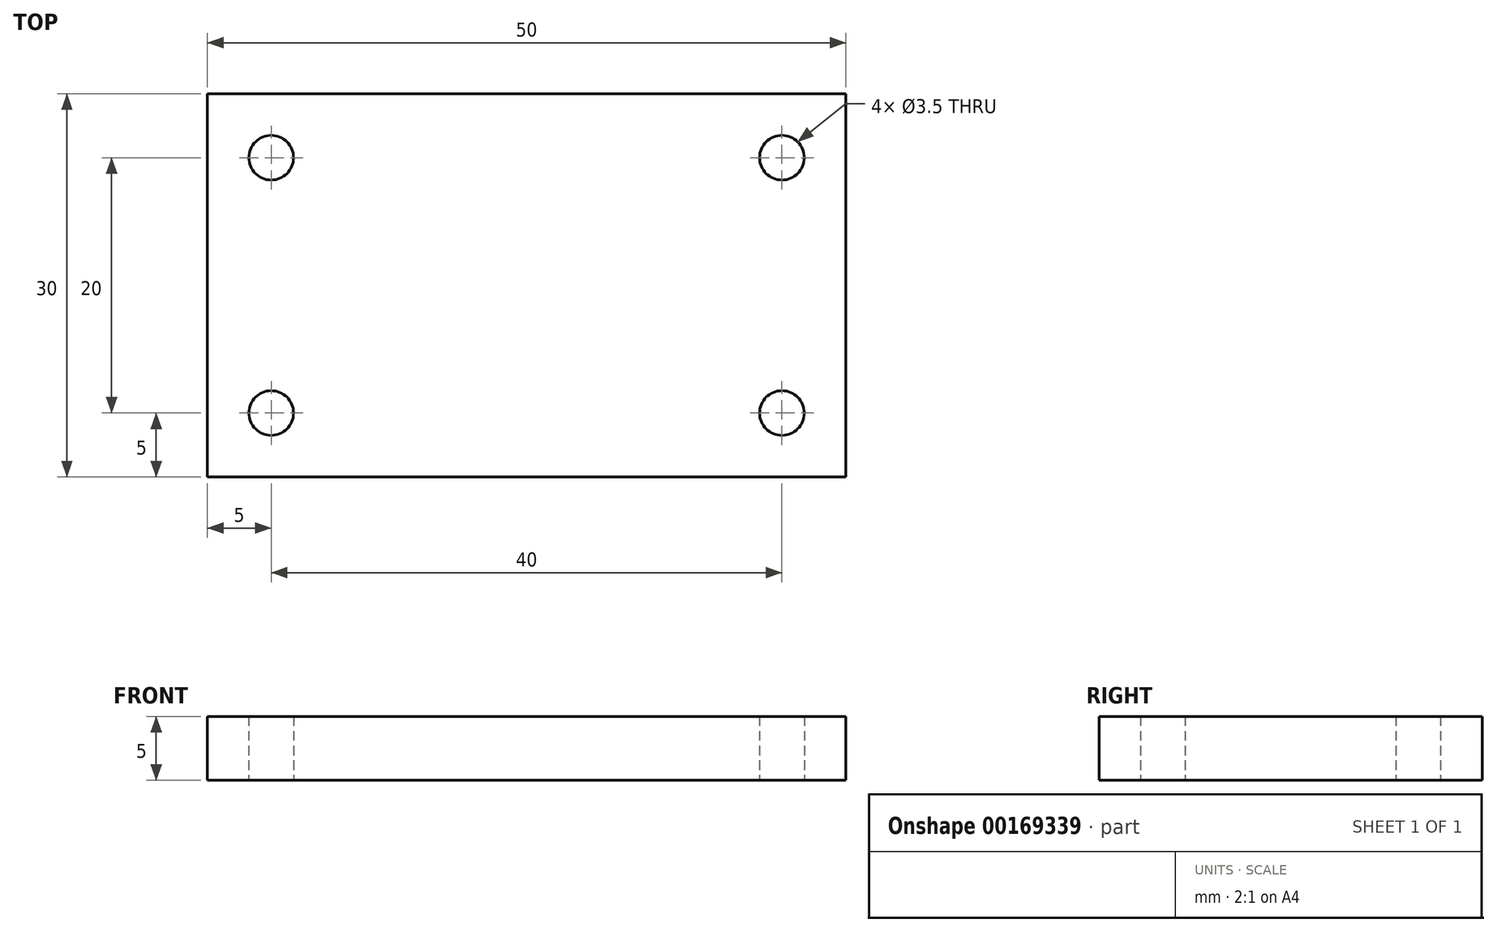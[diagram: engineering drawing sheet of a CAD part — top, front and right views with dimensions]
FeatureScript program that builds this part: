
annotation { "Feature Type Name" : "Feature", "Feature Type Description" : "" }
export const myFeature = defineFeature(function(context is Context, id is Id, definition is map)
    precondition{}
    {
        {
            var Q0;
            Q0=qCreatedBy(makeId("Top.planeOp"),FACE);
            var sketch = newSketch(context, id + "F0", { "sketchPlane" : qUnion([Q0])});
            skLineSegment(sketch, "E0.bottom", {"start": v(25, 15) * mm, "end": v(-25, 15) * mm});
            skLineSegment(sketch, "E0.top", {"start": v(25, -15) * mm, "end": v(-25, -15) * mm});
            skLineSegment(sketch, "E0.left", {"start": v(25, 15) * mm, "end": v(25, -15) * mm});
            skLineSegment(sketch, "E0.right", {"start": v(-25, 15) * mm, "end": v(-25, -15) * mm});
            skPoint(sketch, "E0.middle", {"position": v(0, 0) * mm});
            skCircle(sketch, "E1", {"center": v(-20, -10) * mm, "radius": 1.75 * mm});
            skCircle(sketch, "E2", {"center": v(-20, 10) * mm, "radius": 1.75 * mm});
            skCircle(sketch, "E3", {"center": v(20, 10) * mm, "radius": 1.75 * mm});
            skCircle(sketch, "E4", {"center": v(20, -10) * mm, "radius": 1.75 * mm});
            skSolve(sketch);
        }
        {
            var Q0;
            Q0=makeQuery(id+"F0.imprint","IMPRINT",FACE,{"disambiguationData":[TD([[makeQuery(id+"F0.imprint","IMPRINT",EDGE,{"derivedFrom":sQuery(id+"F0.wireOp",EDGE,"E0.bottom")}),1.0]])]});
            extrude(context, id + "F1", {"entities" : qUnion([Q0]), "depth" : 5 * mm});
        }
    });
